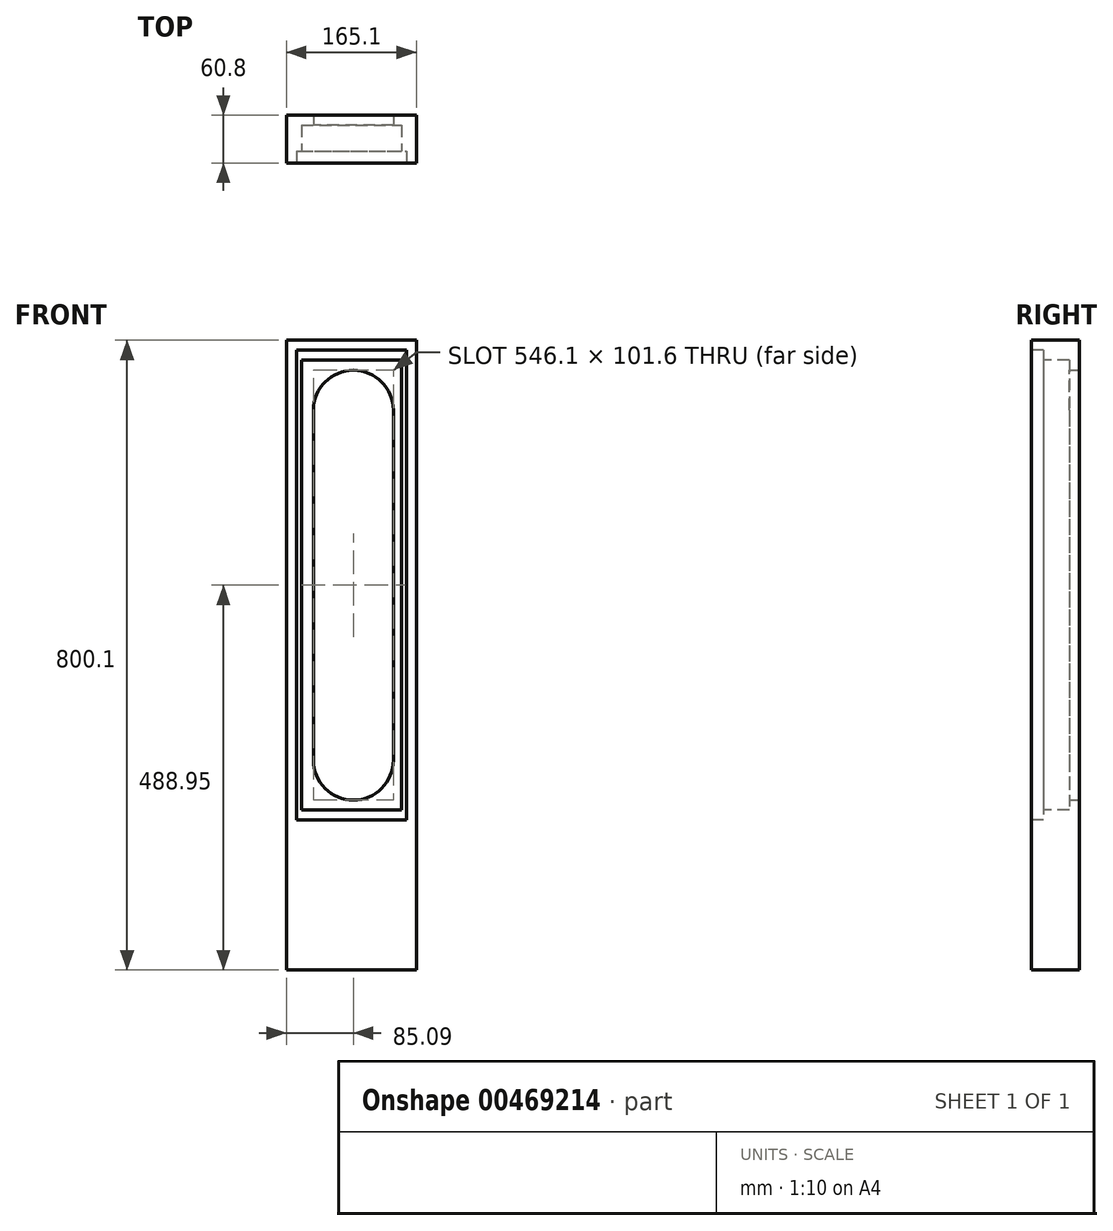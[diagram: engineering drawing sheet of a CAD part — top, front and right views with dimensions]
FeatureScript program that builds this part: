
annotation { "Feature Type Name" : "Feature", "Feature Type Description" : "" }
export const myFeature = defineFeature(function(context is Context, id is Id, definition is map)
    precondition{}
    {
        {
            var Q0;
            Q0=qCreatedBy(makeId("Front.planeOp"),FACE);
            var sketch = newSketch(context, id + "F0", { "sketchPlane" : qUnion([Q0])});
            skLineSegment(sketch, "E0.top", {"start": v(82.55, 609.6) * mm, "end": v(-82.55, 609.6) * mm});
            skLineSegment(sketch, "E0.left", {"start": v(82.55, -190.5) * mm, "end": v(82.55, 609.6) * mm});
            skLineSegment(sketch, "E0.right", {"start": v(-82.55, -190.5) * mm, "end": v(-82.55, 609.6) * mm});
            skPoint(sketch, "E1.middle", {"position": v(0, 0) * mm});
            skLineSegment(sketch, "E2", {"start": v(-82.55, -190.5) * mm, "end": v(82.55, -190.5) * mm});
            skPoint(sketch, "E3.orphan", {"position": v(-82.55, -609.6) * mm});
            skPoint(sketch, "E4.orphan", {"position": v(82.55, -609.6) * mm});
            skLineSegment(sketch, "E5.bottom", {"start": v(-69.85, 596.9) * mm, "end": v(69.85, 596.9) * mm});
            skLineSegment(sketch, "E5.top", {"start": v(-69.85, 0) * mm, "end": v(69.85, 0) * mm});
            skLineSegment(sketch, "E5.left", {"start": v(-69.85, 596.9) * mm, "end": v(-69.85, 0) * mm});
            skLineSegment(sketch, "E5.right", {"start": v(69.85, 596.9) * mm, "end": v(69.85, 0) * mm});
            skLineSegment(sketch, "E6.bottom", {"start": v(-63.5, 584.2) * mm, "end": v(63.5, 584.2) * mm});
            skLineSegment(sketch, "E6.top", {"start": v(-63.5, 12.7) * mm, "end": v(63.5, 12.7) * mm});
            skLineSegment(sketch, "E6.left", {"start": v(-63.5, 584.2) * mm, "end": v(-63.5, 12.7) * mm});
            skLineSegment(sketch, "E6.right", {"start": v(63.5, 584.2) * mm, "end": v(63.5, 12.7) * mm});
            skLineSegment(sketch, "E7.bottom", {"start": v(-48.26, 571.5) * mm, "end": v(53.34, 571.5) * mm});
            skLineSegment(sketch, "E7.top", {"start": v(-48.26, 25.4) * mm, "end": v(53.34, 25.4) * mm});
            skLineSegment(sketch, "E7.left", {"start": v(-48.26, 571.5) * mm, "end": v(-48.26, 25.4) * mm});
            skLineSegment(sketch, "E7.right", {"start": v(53.34, 571.5) * mm, "end": v(53.34, 25.4) * mm});
            skLineSegment(sketch, "E8", {"start": v(0, 755.14) * mm, "end": v(0, -755.14) * mm, "construction": true});
            skSolve(sketch);
        }
        {
            var Q0;
            Q0=makeQuery(id+"F0.imprint","IMPRINT",FACE,{"disambiguationData":[TD([[makeQuery(id+"F0.imprint","IMPRINT",EDGE,{"derivedFrom":sQuery(id+"F0.wireOp",EDGE,"E0.top")}),1.0]])]});
            var Q1;
            Q1=makeQuery(id+"F0.imprint","IMPRINT",FACE,{"disambiguationData":[TD([[makeQuery(id+"F0.imprint","IMPRINT",EDGE,{"derivedFrom":sQuery(id+"F0.wireOp",EDGE,"E1.bottom")}),-1.0]])]});
            var Q2;
            Q2=makeQuery(id+"F0.imprint","IMPRINT",FACE,{"disambiguationData":[TD([[makeQuery(id+"F0.imprint","IMPRINT",EDGE,{"derivedFrom":sQuery(id+"F0.wireOp",EDGE,"l2cz76WN-11cX-8Qg5-Wc74-vKwfhGCtYGeO.bottom")}),-1.0]])]});
            var Q3;
            {var subQ0=sQuery(id+"F0.wireOp",EDGE,"dQK7Thth-TP6K-kbBQ-5Cwl-0GHNaYrmpQfn.left");var subQ1=sQuery(id+"F0.wireOp",EDGE,"E1.bottom");var subQ2=makeQuery(id+"F0.imprint","INTERSECT",VERTEX,{"derivedFrom":[subQ1,subQ0]});Q3=makeQuery(id+"F0.imprint","IMPRINT",FACE,{"disambiguationData":[TD([[makeQuery(id+"F0.imprint","IMPRINT",EDGE,{"disambiguationData":[TD([[subQ2,-1.0]])],"derivedFrom":subQ1}),1.0]])]});}
            var Q4;
            {var subQ5=sQuery(id+"F0.wireOp",EDGE,"huDVYpq4-8GHm-f6ov-cYvV-LWDsyoBmHsaB.top");Q4=makeQuery(id+"F0.imprint","IMPRINT",FACE,{"disambiguationData":[TD([[makeQuery(id+"F0.imprint","IMPRINT",EDGE,{"derivedFrom":subQ5}),1.0]])]});}
            var Q5;
            {var subQ5=sQuery(id+"F0.wireOp",EDGE,"dQK7Thth-TP6K-kbBQ-5Cwl-0GHNaYrmpQfn.bottom");Q5=makeQuery(id+"F0.imprint","IMPRINT",FACE,{"disambiguationData":[TD([[makeQuery(id+"F0.imprint","IMPRINT",EDGE,{"derivedFrom":subQ5}),-1.0]])]});}
            var Q6;
            {var subQ5=sQuery(id+"F0.wireOp",EDGE,"dQK7Thth-TP6K-kbBQ-5Cwl-0GHNaYrmpQfn.top");Q6=makeQuery(id+"F0.imprint","IMPRINT",FACE,{"disambiguationData":[TD([[makeQuery(id+"F0.imprint","IMPRINT",EDGE,{"derivedFrom":subQ5}),1.0]])]});}
            var Q7;
            {var subQ5=sQuery(id+"F0.wireOp",EDGE,"huDVYpq4-8GHm-f6ov-cYvV-LWDsyoBmHsaB.bottom");Q7=makeQuery(id+"F0.imprint","IMPRINT",FACE,{"disambiguationData":[TD([[makeQuery(id+"F0.imprint","IMPRINT",EDGE,{"derivedFrom":subQ5}),-1.0]])]});}
            var Q8;
            {var subQ0=sQuery(id+"F0.wireOp",EDGE,"dQK7Thth-TP6K-kbBQ-5Cwl-0GHNaYrmpQfn.left");var subQ1=sQuery(id+"F0.wireOp",EDGE,"E1.bottom");var subQ2=makeQuery(id+"F0.imprint","INTERSECT",VERTEX,{"derivedFrom":[subQ1,subQ0]});Q8=makeQuery(id+"F0.imprint","IMPRINT",FACE,{"disambiguationData":[TD([[makeQuery(id+"F0.imprint","IMPRINT",EDGE,{"disambiguationData":[TD([[subQ2,-1.0]])],"derivedFrom":subQ1}),-1.0]])]});}
            var Q9;
            Q9=makeQuery(id+"F0.imprint","IMPRINT",FACE,{"disambiguationData":[TD([[makeQuery(id+"F0.imprint","IMPRINT",EDGE,{"derivedFrom":sQuery(id+"F0.wireOp",EDGE,"E6.bottom")}),-1.0]])]});
            var Q10;
            Q10=makeQuery(id+"F0.imprint","IMPRINT",FACE,{"disambiguationData":[TD([[makeQuery(id+"F0.imprint","IMPRINT",EDGE,{"derivedFrom":sQuery(id+"F0.wireOp",EDGE,"E5.bottom")}),-1.0]])]});
            extrude(context, id + "F1", {"entities" : qUnion([Q0, Q1, Q2, Q3, Q4, Q5, Q6, Q7, Q8, Q9, Q10]), "oppositeDirection" : true, "depth" : 50.8 * mm});
        }
        {
            var Q0;
            Q0=makeQuery(id+"F0.imprint","IMPRINT",FACE,{"disambiguationData":[TD([[makeQuery(id+"F0.imprint","IMPRINT",EDGE,{"derivedFrom":sQuery(id+"F0.wireOp",EDGE,"E5.bottom")}),-1.0]])]});
            extrude(context, id + "F2", {"entities" : qUnion([Q0]), "operationType" : NewBodyOperationType.REMOVE, "oppositeDirection" : true, "depth" : 5 * mm});
        }
        {
            var Q0;
            Q0=makeQuery(id+"F0.imprint","IMPRINT",FACE,{"disambiguationData":[TD([[makeQuery(id+"F0.imprint","IMPRINT",EDGE,{"derivedFrom":sQuery(id+"F0.wireOp",EDGE,"E6.bottom")}),-1.0]])]});
            extrude(context, id + "F3", {"entities" : qUnion([Q0]), "operationType" : NewBodyOperationType.REMOVE, "oppositeDirection" : true, "depth" : 38.1 * mm});
        }
        {
            var Q0;
            Q0=makeQuery(id+"F1.opExtrude","SWEPT_EDGE",EDGE,{"disambiguationData":[OSD([sQuery(id+"F0.wireOp",EDGE,"E7.bottom"),sQuery(id+"F0.wireOp",EDGE,"E7.right")])]});
            var Q1;
            Q1=makeQuery(id+"F1.opExtrude","SWEPT_EDGE",EDGE,{"disambiguationData":[OSD([sQuery(id+"F0.wireOp",EDGE,"E7.bottom"),sQuery(id+"F0.wireOp",EDGE,"E7.left")])]});
            var Q2;
            Q2=makeQuery(id+"F1.opExtrude","SWEPT_EDGE",EDGE,{"disambiguationData":[OSD([sQuery(id+"F0.wireOp",EDGE,"E7.top"),sQuery(id+"F0.wireOp",EDGE,"E7.left")])]});
            var Q3;
            Q3=makeQuery(id+"F1.opExtrude","SWEPT_EDGE",EDGE,{"disambiguationData":[OSD([sQuery(id+"F0.wireOp",EDGE,"E7.top"),sQuery(id+"F0.wireOp",EDGE,"E7.right")])]});
            fillet(context, id + "F4", {"entities" : qUnion([Q0, Q1, Q2, Q3]), "radius" : 50.8 * mm, "tangentPropagation" : true, "allowEdgeOverflow" : false});
        }
        {
            var Q0;
            Q0=qSketchRegion(id+"F0",true);
            var Q1;
            {var subQ0=sQuery(id+"F0.wireOp",EDGE,"E0.right");var subQ1=sQuery(id+"F0.wireOp",EDGE,"E0.left");var subQ2=sQuery(id+"F0.wireOp",EDGE,"E2");var subQ3=sQuery(id+"F0.wireOp",EDGE,"E0.top");Q1=makeQuery(id+"F2.boolean.opBoolean","SPLIT",FACE,{"disambiguationData":[TD([makeQuery(id+"F1.opExtrude","SWEPT_FACE",FACE,{"disambiguationData":[OSD([subQ3])]})])],"derivedFrom":makeQuery(id+"F1.opExtrude","CAP_FACE",FACE,{"disambiguationData":[OSD([subQ3,subQ1,subQ0,subQ2,sQuery(id+"F0.wireOp",EDGE,"E7.bottom"),sQuery(id+"F0.wireOp",EDGE,"E7.top"),sQuery(id+"F0.wireOp",EDGE,"E7.left"),sQuery(id+"F0.wireOp",EDGE,"E7.right")])],"isStart":true})});}
            extrude(context, id + "F5", {"entities" : qUnion([Q0, Q1]), "operationType" : NewBodyOperationType.ADD, "depth" : 10 * mm});
        }
    });
